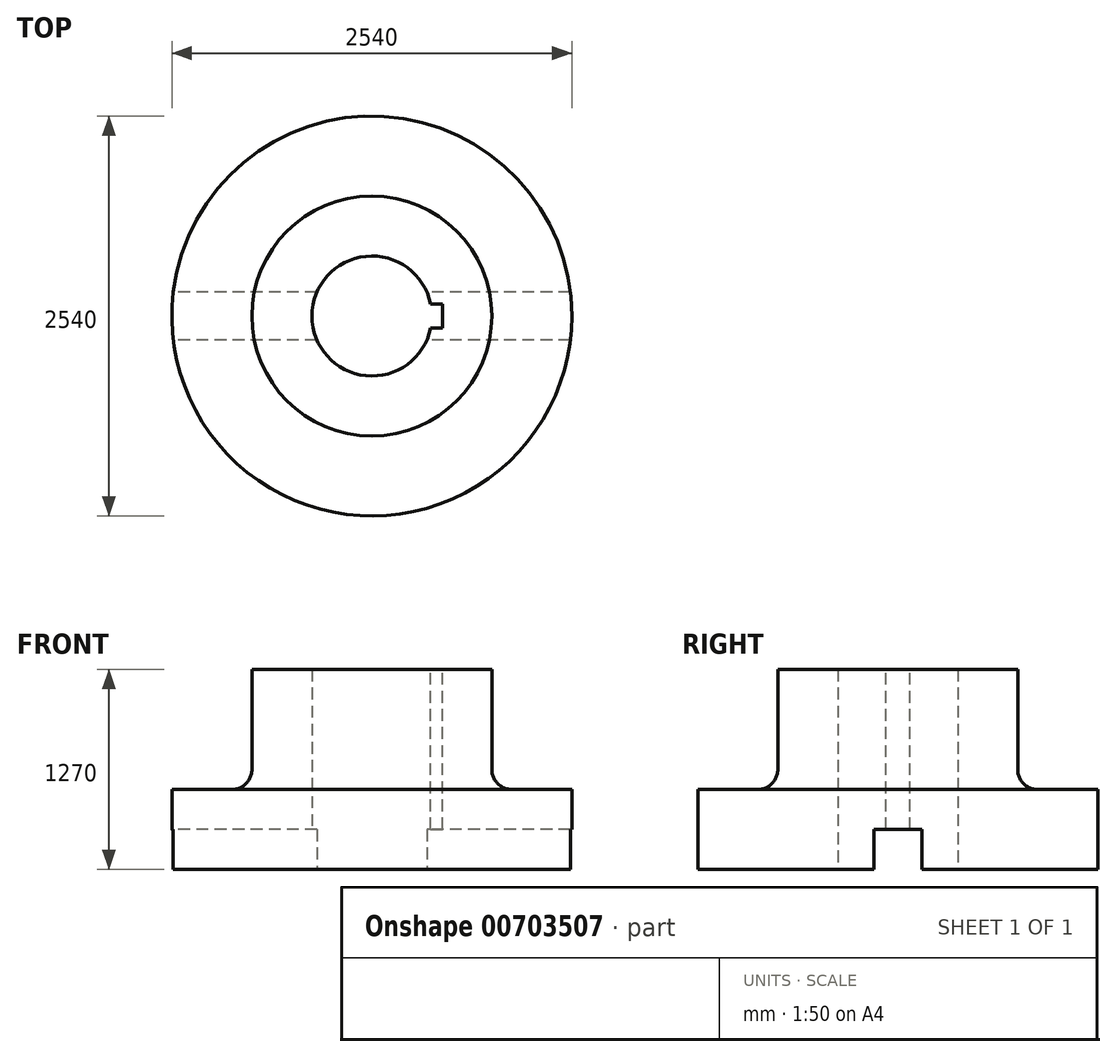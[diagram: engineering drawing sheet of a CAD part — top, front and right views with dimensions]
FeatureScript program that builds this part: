
annotation { "Feature Type Name" : "Feature", "Feature Type Description" : "" }
export const myFeature = defineFeature(function(context is Context, id is Id, definition is map)
    precondition{}
    {
        {
            var Q0;
            Q0=qCreatedBy(makeId("Top.planeOp"),FACE);
            var sketch = newSketch(context, id + "F0", { "sketchPlane" : qUnion([Q0])});
            skCircle(sketch, "E0", {"center": v(0, 0) * mm, "radius": 381 * mm});
            skCircle(sketch, "E1", {"center": v(0, 0) * mm, "radius": 762 * mm});
            skCircle(sketch, "E2", {"center": v(0, 0) * mm, "radius": 1270 * mm});
            skSolve(sketch);
        }
        {
            var Q0;
            Q0=makeQuery(id+"F0.imprint","IMPRINT",FACE,{"disambiguationData":[TD([[makeQuery(id+"F0.imprint","IMPRINT",EDGE,{"derivedFrom":sQuery(id+"F0.wireOp",EDGE,"E0")}),-1.0]])]});
            extrude(context, id + "F1", {"entities" : qUnion([Q0]), "depth" : 1270 * mm, "offsetDistance" : 25.4 * mm});
        }
        {
            var Q0;
            Q0=qCreatedBy(makeId("Top.planeOp"),FACE);
            var sketch = newSketch(context, id + "F2", { "sketchPlane" : qUnion([Q0])});
            skCircle(sketch, "E3", {"center": v(0, 0) * mm, "radius": 1270 * mm});
            skSolve(sketch);
        }
        {
            var Q0;
            Q0=makeQuery(id+"F2.imprint","IMPRINT",FACE,{"disambiguationData":[TD([[makeQuery(id+"F2.imprint","IMPRINT",EDGE,{"derivedFrom":sQuery(id+"F2.wireOp",EDGE,"E3")}),1.0]])]});
            extrude(context, id + "F3", {"entities" : qUnion([Q0]), "operationType" : NewBodyOperationType.ADD, "depth" : 508 * mm, "offsetDistance" : 25.4 * mm});
        }
        {
            var Q0;
            Q0=makeQuery(id+"F3.boolean.opBoolean","SPLIT",FACE,{"disambiguationData":[TD([makeQuery(id+"F1.opExtrude","SWEPT_FACE",FACE,{"disambiguationData":[OSD([sQuery(id+"F0.wireOp",EDGE,"E0")])]})])],"derivedFrom":makeQuery(id+"F3.opExtrude","CAP_FACE",FACE,{"disambiguationData":[OSD([sQuery(id+"F2.wireOp",EDGE,"E3")])],"isStart":false})});
            extrude(context, id + "F4", {"entities" : qUnion([Q0]), "operationType" : NewBodyOperationType.REMOVE, "oppositeDirection" : true, "depth" : 1582.42 * mm, "offsetDistance" : 25.4 * mm});
        }
        {
            var Q0;
            Q0=makeQuery(id+"F1.opExtrude","CAP_FACE",FACE,{"disambiguationData":[OSD([sQuery(id+"F0.wireOp",EDGE,"E0"),sQuery(id+"F0.wireOp",EDGE,"E1")])],"isStart":false});
            var sketch = newSketch(context, id + "F5", { "sketchPlane" : qUnion([Q0])});
            skLineSegment(sketch, "E4", {"start": v(381, 0) * mm, "end": v(431.8, 0) * mm});
            skLineSegment(sketch, "E5", {"start": v(431.8, 0) * mm, "end": v(431.8, 76.2) * mm});
            skLineSegment(sketch, "E6", {"start": v(431.8, 76.2) * mm, "end": v(373.3, 76.2) * mm});
            skLineSegment(sketch, "E7", {"start": v(373.3, 76.2) * mm, "end": v(373.3, -76.2) * mm});
            skLineSegment(sketch, "E8", {"start": v(373.3, -76.2) * mm, "end": v(449.5, -76.2) * mm});
            skLineSegment(sketch, "E9", {"start": v(449.5, -76.2) * mm, "end": v(449.5, 76.2) * mm});
            skLineSegment(sketch, "E10", {"start": v(449.5, 76.2) * mm, "end": v(431.8, 76.2) * mm});
            skSolve(sketch);
        }
        {
            var Q0;
            {var subQ1=sQuery(id+"F5.wireOp",EDGE,"E4");Q0=makeQuery(id+"F5.imprint","IMPRINT",FACE,{"disambiguationData":[TD([[makeQuery(id+"F5.imprint","IMPRINT",EDGE,{"derivedFrom":subQ1}),-1.0]])]});}
            var Q1;
            {var subQ0=sQuery(id+"F5.wireOp",EDGE,"E4");Q1=makeQuery(id+"F5.imprint","IMPRINT",FACE,{"disambiguationData":[TD([[makeQuery(id+"F5.imprint","IMPRINT",EDGE,{"derivedFrom":subQ0}),1.0]])]});}
            var Q2;
            {var subQ0=sQuery(id+"F5.wireOp",EDGE,"E7");Q2=makeQuery(id+"F5.imprint","IMPRINT",FACE,{"disambiguationData":[TD([[makeQuery(id+"F5.imprint","IMPRINT",EDGE,{"derivedFrom":subQ0}),1.0]])]});}
            extrude(context, id + "F6", {"entities" : qUnion([Q0, Q1, Q2]), "operationType" : NewBodyOperationType.REMOVE, "oppositeDirection" : true, "depth" : 1351.28 * mm, "offsetDistance" : 25.4 * mm});
        }
        {
            var Q0;
            Q0=makeQuery(id+"F3.boolean.opBoolean","MERGE",FACE,{"derivedFrom":[makeQuery(id+"F1.opExtrude","CAP_FACE",FACE,{"disambiguationData":[OSD([sQuery(id+"F0.wireOp",EDGE,"E0"),sQuery(id+"F0.wireOp",EDGE,"E1")])],"isStart":true}),makeQuery(id+"F3.opExtrude","CAP_FACE",FACE,{"disambiguationData":[OSD([sQuery(id+"F2.wireOp",EDGE,"E3")])],"isStart":true})]});
            var sketch = newSketch(context, id + "F7", { "sketchPlane" : qUnion([Q0])});
            skPoint(sketch, "E11.firstSnap0", {"position": v(449.5, 0) * mm});
            skLineSegment(sketch, "E11.bottom", {"start": v(1270, 0) * mm, "end": v(-1270, 0) * mm});
            skLineSegment(sketch, "E11.top", {"start": v(1270, 152.4) * mm, "end": v(-1270, 152.4) * mm});
            skLineSegment(sketch, "E11.left", {"start": v(1270, 0) * mm, "end": v(1270, 152.4) * mm});
            skLineSegment(sketch, "E11.right", {"start": v(-1270, 0) * mm, "end": v(-1270, 152.4) * mm});
            skLineSegment(sketch, "E12.top", {"start": v(1270, -152.4) * mm, "end": v(-1270, -152.4) * mm});
            skLineSegment(sketch, "E12.left", {"start": v(1270, 0) * mm, "end": v(1270, -152.4) * mm});
            skLineSegment(sketch, "E12.right", {"start": v(-1270, 0) * mm, "end": v(-1270, -152.4) * mm});
            skSolve(sketch);
        }
        {
            var Q0;
            {var subQ0=sQuery(id+"F7.wireOp",EDGE,"E11.left");Q0=makeQuery(id+"F7.imprint","IMPRINT",FACE,{"disambiguationData":[TD([[makeQuery(id+"F7.imprint","IMPRINT",EDGE,{"derivedFrom":subQ0}),1.0]])]});}
            var Q1;
            {var subQ0=sQuery(id+"F7.wireOp",EDGE,"E11.right");Q1=makeQuery(id+"F7.imprint","IMPRINT",FACE,{"disambiguationData":[TD([[makeQuery(id+"F7.imprint","IMPRINT",EDGE,{"derivedFrom":subQ0}),-1.0]])]});}
            var Q2;
            {var subQ0=sQuery(id+"F7.wireOp",EDGE,"E12.left");Q2=makeQuery(id+"F7.imprint","IMPRINT",FACE,{"disambiguationData":[TD([[makeQuery(id+"F7.imprint","IMPRINT",EDGE,{"derivedFrom":subQ0}),-1.0]])]});}
            var Q3;
            {var subQ0=sQuery(id+"F7.wireOp",EDGE,"E12.right");var subQ1=sQuery(id+"F7.wireOp",EDGE,"E12.top");var subQ2=makeQuery(id+"F7.imprint","INTERSECT",VERTEX,{"derivedFrom":[subQ1,subQ0]});Q3=makeQuery(id+"F7.imprint","IMPRINT",FACE,{"disambiguationData":[TD([[makeQuery(id+"F7.imprint","IMPRINT",EDGE,{"disambiguationData":[TD([[subQ2,1.0]])],"derivedFrom":subQ1}),-1.0]])]});}
            var Q4;
            {var subQ0=sQuery(id+"F7.wireOp",EDGE,"E11.bottom");Q4=makeQuery(id+"F7.imprint","IMPRINT",FACE,{"disambiguationData":[TD([[makeQuery(id+"F7.imprint","IMPRINT",EDGE,{"derivedFrom":subQ0}),-1.0]])]});}
            var Q5;
            {var subQ0=sQuery(id+"F7.wireOp",EDGE,"E12.top");var subQ1=sQuery(id+"F2.wireOp",EDGE,"E3");var subQ2=makeQuery(id+"F3.opExtrude","CAP_EDGE",EDGE,{"disambiguationData":[OSD([subQ1])],"isStart":true});var subQ3=makeQuery(id+"F7.imprint","INTERSECT",VERTEX,{"disambiguationData":[OD(1.0)],"derivedFrom":[subQ2,subQ0]});Q5=makeQuery(id+"F7.imprint","IMPRINT",FACE,{"disambiguationData":[TD([[makeQuery(id+"F7.imprint","IMPRINT",EDGE,{"disambiguationData":[TD([[subQ3,-1.0]])],"derivedFrom":subQ2}),-1.0]])]});}
            var Q6;
            {var subQ0=sQuery(id+"F2.wireOp",EDGE,"E3");var subQ1=sQuery(id+"F0.wireOp",EDGE,"E0");var subQ2=makeQuery(id+"F3.boolean.opBoolean","MERGE",FACE,{"derivedFrom":[makeQuery(id+"F1.opExtrude","CAP_FACE",FACE,{"disambiguationData":[OSD([subQ1,sQuery(id+"F0.wireOp",EDGE,"E1")])],"isStart":true}),makeQuery(id+"F3.opExtrude","CAP_FACE",FACE,{"disambiguationData":[OSD([subQ0])],"isStart":true})]});var subQ3=subQ2;var subQ4=makeQuery(id+"F6.boolean.opBoolean","INTERSECT",EDGE,{"derivedFrom":[subQ3,makeQuery(id+"F6.opExtrude","SWEPT_FACE",FACE,{"disambiguationData":[OSD([sQuery(id+"F5.wireOp",EDGE,"E8")])]})]});Q6=makeQuery(id+"F7.imprint","IMPRINT",FACE,{"disambiguationData":[TD([[makeQuery(id+"F7.imprint","IMPRINT",EDGE,{"derivedFrom":subQ4}),-1.0]])]});}
            var Q7;
            {var subQ0=sQuery(id+"F2.wireOp",EDGE,"E3");var subQ1=sQuery(id+"F0.wireOp",EDGE,"E0");var subQ2=makeQuery(id+"F3.boolean.opBoolean","MERGE",FACE,{"derivedFrom":[makeQuery(id+"F1.opExtrude","CAP_FACE",FACE,{"disambiguationData":[OSD([subQ1,sQuery(id+"F0.wireOp",EDGE,"E1")])],"isStart":true}),makeQuery(id+"F3.opExtrude","CAP_FACE",FACE,{"disambiguationData":[OSD([subQ0])],"isStart":true})]});var subQ3=subQ2;var subQ4=makeQuery(id+"F6.boolean.opBoolean","INTERSECT",EDGE,{"derivedFrom":[subQ3,makeQuery(id+"F6.opExtrude","SWEPT_FACE",FACE,{"disambiguationData":[OSD([sQuery(id+"F5.wireOp",EDGE,"E6"),sQuery(id+"F5.wireOp",EDGE,"E10")])]})]});Q7=makeQuery(id+"F7.imprint","IMPRINT",FACE,{"disambiguationData":[TD([[makeQuery(id+"F7.imprint","IMPRINT",EDGE,{"derivedFrom":subQ4}),1.0]])]});}
            var Q8;
            {var subQ1=sQuery(id+"F2.wireOp",EDGE,"E3");var subQ2=sQuery(id+"F0.wireOp",EDGE,"E0");var subQ3=makeQuery(id+"F3.boolean.opBoolean","MERGE",FACE,{"derivedFrom":[makeQuery(id+"F1.opExtrude","CAP_FACE",FACE,{"disambiguationData":[OSD([subQ2,sQuery(id+"F0.wireOp",EDGE,"E1")])],"isStart":true}),makeQuery(id+"F3.opExtrude","CAP_FACE",FACE,{"disambiguationData":[OSD([subQ1])],"isStart":true})]});var subQ7=subQ3;var subQ8=makeQuery(id+"F6.boolean.opBoolean","INTERSECT",EDGE,{"derivedFrom":[subQ7,makeQuery(id+"F6.opExtrude","SWEPT_FACE",FACE,{"disambiguationData":[OSD([sQuery(id+"F5.wireOp",EDGE,"E6"),sQuery(id+"F5.wireOp",EDGE,"E10")])]})]});Q8=makeQuery(id+"F7.imprint","IMPRINT",FACE,{"disambiguationData":[TD([[makeQuery(id+"F7.imprint","IMPRINT",EDGE,{"derivedFrom":subQ8}),-1.0]])]});}
            var Q9;
            {var subQ0=sQuery(id+"F2.wireOp",EDGE,"E3");var subQ1=sQuery(id+"F0.wireOp",EDGE,"E0");var subQ2=makeQuery(id+"F3.boolean.opBoolean","MERGE",FACE,{"derivedFrom":[makeQuery(id+"F1.opExtrude","CAP_FACE",FACE,{"disambiguationData":[OSD([subQ1,sQuery(id+"F0.wireOp",EDGE,"E1")])],"isStart":true}),makeQuery(id+"F3.opExtrude","CAP_FACE",FACE,{"disambiguationData":[OSD([subQ0])],"isStart":true})]});var subQ3=subQ2;var subQ4=makeQuery(id+"F6.boolean.opBoolean","INTERSECT",EDGE,{"derivedFrom":[subQ3,makeQuery(id+"F6.opExtrude","SWEPT_FACE",FACE,{"disambiguationData":[OSD([sQuery(id+"F5.wireOp",EDGE,"E8")])]})]});Q9=makeQuery(id+"F7.imprint","IMPRINT",FACE,{"disambiguationData":[TD([[makeQuery(id+"F7.imprint","IMPRINT",EDGE,{"derivedFrom":subQ4}),1.0]])]});}
            extrude(context, id + "F8", {"entities" : qUnion([Q0, Q1, Q2, Q3, Q4, Q5, Q6, Q7, Q8, Q9]), "operationType" : NewBodyOperationType.REMOVE, "oppositeDirection" : true, "depth" : 254 * mm, "offsetDistance" : 25.4 * mm});
        }
        {
            var Q0;
            {var subQ0=sQuery(id+"F7.wireOp",EDGE,"E11.left");Q0=makeQuery(id+"F7.imprint","IMPRINT",FACE,{"disambiguationData":[TD([[makeQuery(id+"F7.imprint","IMPRINT",EDGE,{"derivedFrom":subQ0}),1.0]])]});}
            var Q1;
            {var subQ0=sQuery(id+"F7.wireOp",EDGE,"E11.right");Q1=makeQuery(id+"F7.imprint","IMPRINT",FACE,{"disambiguationData":[TD([[makeQuery(id+"F7.imprint","IMPRINT",EDGE,{"derivedFrom":subQ0}),-1.0]])]});}
            var Q2;
            {var subQ0=sQuery(id+"F7.wireOp",EDGE,"E12.left");Q2=makeQuery(id+"F7.imprint","IMPRINT",FACE,{"disambiguationData":[TD([[makeQuery(id+"F7.imprint","IMPRINT",EDGE,{"derivedFrom":subQ0}),-1.0]])]});}
            var Q3;
            {var subQ0=sQuery(id+"F7.wireOp",EDGE,"E12.right");Q3=makeQuery(id+"F7.imprint","IMPRINT",FACE,{"disambiguationData":[TD([[makeQuery(id+"F7.imprint","IMPRINT",EDGE,{"derivedFrom":subQ0}),1.0]])]});}
            var Q4;
            {var subQ0=sQuery(id+"F2.wireOp",EDGE,"E3");var subQ1=sQuery(id+"F0.wireOp",EDGE,"E0");var subQ2=makeQuery(id+"F3.boolean.opBoolean","MERGE",FACE,{"derivedFrom":[makeQuery(id+"F1.opExtrude","CAP_FACE",FACE,{"disambiguationData":[OSD([subQ1,sQuery(id+"F0.wireOp",EDGE,"E1")])],"isStart":true}),makeQuery(id+"F3.opExtrude","CAP_FACE",FACE,{"disambiguationData":[OSD([subQ0])],"isStart":true})]});var subQ3=subQ2;var subQ4=makeQuery(id+"F6.boolean.opBoolean","INTERSECT",EDGE,{"derivedFrom":[subQ3,makeQuery(id+"F6.opExtrude","SWEPT_FACE",FACE,{"disambiguationData":[OSD([sQuery(id+"F5.wireOp",EDGE,"E8")])]})]});Q4=makeQuery(id+"F7.imprint","IMPRINT",FACE,{"disambiguationData":[TD([[makeQuery(id+"F7.imprint","IMPRINT",EDGE,{"derivedFrom":subQ4}),1.0]])]});}
            var Q5;
            {var subQ0=sQuery(id+"F2.wireOp",EDGE,"E3");var subQ1=sQuery(id+"F0.wireOp",EDGE,"E0");var subQ2=makeQuery(id+"F3.boolean.opBoolean","MERGE",FACE,{"derivedFrom":[makeQuery(id+"F1.opExtrude","CAP_FACE",FACE,{"disambiguationData":[OSD([subQ1,sQuery(id+"F0.wireOp",EDGE,"E1")])],"isStart":true}),makeQuery(id+"F3.opExtrude","CAP_FACE",FACE,{"disambiguationData":[OSD([subQ0])],"isStart":true})]});var subQ3=subQ2;var subQ4=makeQuery(id+"F6.boolean.opBoolean","INTERSECT",EDGE,{"derivedFrom":[subQ3,makeQuery(id+"F6.opExtrude","SWEPT_FACE",FACE,{"disambiguationData":[OSD([sQuery(id+"F5.wireOp",EDGE,"E8")])]})]});Q5=makeQuery(id+"F7.imprint","IMPRINT",FACE,{"disambiguationData":[TD([[makeQuery(id+"F7.imprint","IMPRINT",EDGE,{"derivedFrom":subQ4}),-1.0]])]});}
            var Q6;
            {var subQ0=sQuery(id+"F2.wireOp",EDGE,"E3");var subQ1=sQuery(id+"F0.wireOp",EDGE,"E0");var subQ2=makeQuery(id+"F3.boolean.opBoolean","MERGE",FACE,{"derivedFrom":[makeQuery(id+"F1.opExtrude","CAP_FACE",FACE,{"disambiguationData":[OSD([subQ1,sQuery(id+"F0.wireOp",EDGE,"E1")])],"isStart":true}),makeQuery(id+"F3.opExtrude","CAP_FACE",FACE,{"disambiguationData":[OSD([subQ0])],"isStart":true})]});var subQ3=subQ2;var subQ4=makeQuery(id+"F6.boolean.opBoolean","INTERSECT",EDGE,{"derivedFrom":[subQ3,makeQuery(id+"F6.opExtrude","SWEPT_FACE",FACE,{"disambiguationData":[OSD([sQuery(id+"F5.wireOp",EDGE,"E6"),sQuery(id+"F5.wireOp",EDGE,"E10")])]})]});Q6=makeQuery(id+"F7.imprint","IMPRINT",FACE,{"disambiguationData":[TD([[makeQuery(id+"F7.imprint","IMPRINT",EDGE,{"derivedFrom":subQ4}),1.0]])]});}
            var Q7;
            {var subQ0=sQuery(id+"F2.wireOp",EDGE,"E3");var subQ1=sQuery(id+"F0.wireOp",EDGE,"E0");var subQ2=makeQuery(id+"F3.boolean.opBoolean","MERGE",FACE,{"derivedFrom":[makeQuery(id+"F1.opExtrude","CAP_FACE",FACE,{"disambiguationData":[OSD([subQ1,sQuery(id+"F0.wireOp",EDGE,"E1")])],"isStart":true}),makeQuery(id+"F3.opExtrude","CAP_FACE",FACE,{"disambiguationData":[OSD([subQ0])],"isStart":true})]});var subQ3=subQ2;var subQ4=makeQuery(id+"F6.boolean.opBoolean","INTERSECT",EDGE,{"derivedFrom":[subQ3,makeQuery(id+"F6.opExtrude","SWEPT_FACE",FACE,{"disambiguationData":[OSD([sQuery(id+"F5.wireOp",EDGE,"E6"),sQuery(id+"F5.wireOp",EDGE,"E10")])]})]});Q7=makeQuery(id+"F7.imprint","IMPRINT",FACE,{"disambiguationData":[TD([[makeQuery(id+"F7.imprint","IMPRINT",EDGE,{"derivedFrom":subQ4}),-1.0]])]});}
            var Q8;
            {var subQ0=sQuery(id+"F7.wireOp",EDGE,"E11.top");var subQ1=sQuery(id+"F2.wireOp",EDGE,"E3");var subQ2=makeQuery(id+"F3.opExtrude","CAP_EDGE",EDGE,{"disambiguationData":[OSD([subQ1])],"isStart":true});var subQ3=makeQuery(id+"F7.imprint","INTERSECT",VERTEX,{"disambiguationData":[OD(1.0)],"derivedFrom":[subQ2,subQ0]});Q8=makeQuery(id+"F7.imprint","IMPRINT",FACE,{"disambiguationData":[TD([[makeQuery(id+"F7.imprint","IMPRINT",EDGE,{"disambiguationData":[TD([[subQ3,1.0]])],"derivedFrom":subQ2}),-1.0]])]});}
            extrude(context, id + "F9", {"entities" : qUnion([Q0, Q1, Q2, Q3, Q4, Q5, Q6, Q7, Q8]), "operationType" : NewBodyOperationType.REMOVE, "oppositeDirection" : true, "depth" : 254 * mm, "offsetDistance" : 25.4 * mm});
        }
        {
            var Q0;
            Q0=makeQuery(id+"F3.boolean.opBoolean","INTERSECT",EDGE,{"derivedFrom":[makeQuery(id+"F1.opExtrude","SWEPT_FACE",FACE,{"disambiguationData":[OSD([sQuery(id+"F0.wireOp",EDGE,"E1")])]}),makeQuery(id+"F3.opExtrude","CAP_FACE",FACE,{"disambiguationData":[OSD([sQuery(id+"F2.wireOp",EDGE,"E3")])],"isStart":false})]});
            fillet(context, id + "F10", {"entities" : qUnion([Q0]), "radius" : 127 * mm, "tangentPropagation" : true, "allowEdgeOverflow" : false});
        }
    });
